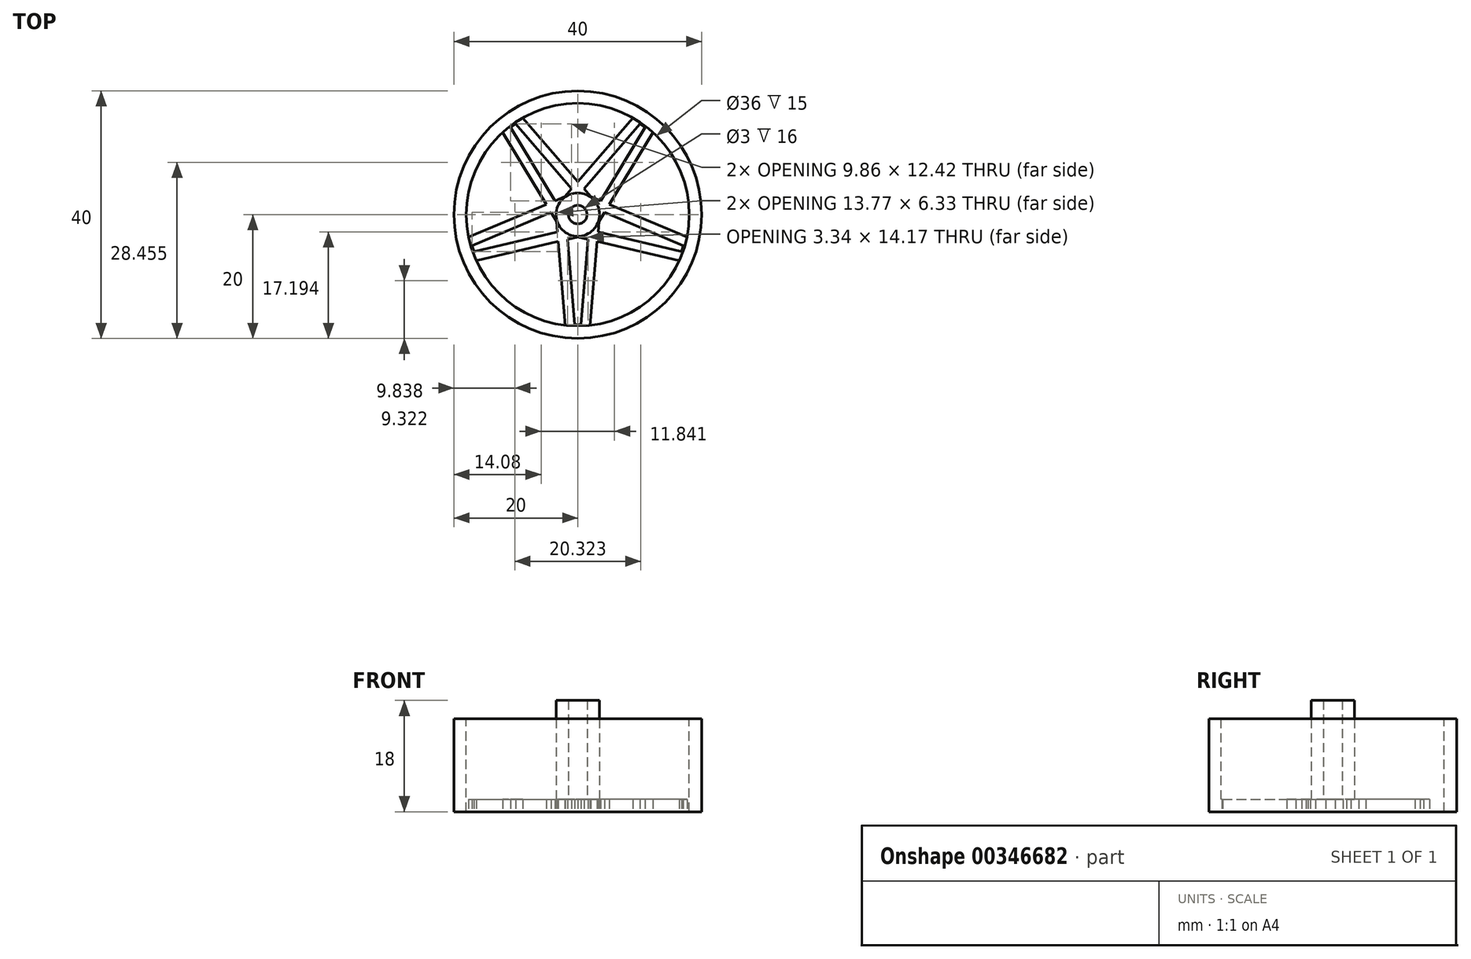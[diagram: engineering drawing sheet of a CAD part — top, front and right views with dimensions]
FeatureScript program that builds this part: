
annotation { "Feature Type Name" : "Feature", "Feature Type Description" : "" }
export const myFeature = defineFeature(function(context is Context, id is Id, definition is map)
    precondition{}
    {
        {
            var Q0;
            Q0=qCreatedBy(makeId("Top.planeOp"),FACE);
            var sketch = newSketch(context, id + "F0", { "sketchPlane" : qUnion([Q0])});
            skCircle(sketch, "E0", {"center": v(0, 0) * mm, "radius": 20 * mm});
            skSolve(sketch);
        }
        {
            var Q0;
            Q0=makeQuery(id+"F0.imprint","IMPRINT",FACE,{"disambiguationData":[TD([[makeQuery(id+"F0.imprint","IMPRINT",EDGE,{"derivedFrom":sQuery(id+"F0.wireOp",EDGE,"E0")}),1.0]])]});
            extrude(context, id + "F1", {"entities" : qUnion([Q0]), "depth" : 15 * mm});
        }
        {
            var Q0;
            Q0=makeQuery(id+"F1.opExtrude","CAP_FACE",FACE,{"disambiguationData":[OSD([sQuery(id+"F0.wireOp",EDGE,"E0")])],"isStart":false});
            var sketch = newSketch(context, id + "F2", { "sketchPlane" : qUnion([Q0])});
            skCircle(sketch, "E1", {"center": v(0, 0) * mm, "radius": 18 * mm});
            skSolve(sketch);
        }
        {
            var Q0;
            Q0=makeQuery(id+"F2.imprint","IMPRINT",FACE,{"disambiguationData":[TD([[makeQuery(id+"F2.imprint","IMPRINT",EDGE,{"derivedFrom":sQuery(id+"F2.wireOp",EDGE,"E1")}),1.0]])]});
            extrude(context, id + "F3", {"entities" : qUnion([Q0]), "operationType" : NewBodyOperationType.REMOVE, "oppositeDirection" : true, "depth" : 13 * mm});
        }
        {
            var Q0;
            Q0=makeQuery(id+"F3.boolean.opBoolean","COPY",FACE,{"derivedFrom":makeQuery(id+"F3.opExtrude","CAP_FACE",FACE,{"disambiguationData":[OSD([sQuery(id+"F2.wireOp",EDGE,"E1")])],"isStart":false})});
            var sketch = newSketch(context, id + "F4", { "sketchPlane" : qUnion([Q0])});
            skCircle(sketch, "E2", {"center": v(0, 0) * mm, "radius": 1.5 * mm});
            skCircle(sketch, "E3", {"center": v(0, 0) * mm, "radius": 3.5 * mm});
            skSolve(sketch);
        }
        {
            var Q0;
            Q0=makeQuery(id+"F1.opExtrude","CAP_FACE",FACE,{"disambiguationData":[OSD([sQuery(id+"F0.wireOp",EDGE,"E0")])],"isStart":true});
            var sketch = newSketch(context, id + "F5", { "sketchPlane" : qUnion([Q0])});
            skArc(sketch, "E4", {"start": v(-2, 17.89) * mm, "mid": v(-10.58, 14.56) * mm, "end": v(-16.4, 7.43) * mm});
            skLineSegment(sketch, "E5", {"start": v(0, 0) * mm, "end": v(2, 0) * mm});
            skLineSegment(sketch, "E6", {"start": v(2, 17.89) * mm, "end": v(3.15, 4.33) * mm});
            skLineSegment(sketch, "E7.MirrorCS", {"start": v(-2, 17.89) * mm, "end": v(-3.15, 4.33) * mm});
            skLineSegment(sketch, "E8.0", {"start": v(-0.5, 17.76) * mm, "end": v(-1.67, 3.99) * mm});
            skLineSegment(sketch, "E9.0", {"start": v(0.5, 17.76) * mm, "end": v(1.67, 3.99) * mm});
            skLineSegment(sketch, "E10", {"start": v(-0.5, 17.76) * mm, "end": v(0.5, 17.76) * mm});
            skLineSegment(sketch, "E11.1.0", {"start": v(-17.63, 3.63) * mm, "end": v(-5.1, -1.65) * mm});
            skLineSegment(sketch, "E11.1.1", {"start": v(-17.05, 5) * mm, "end": v(-4.3, -0.36) * mm});
            skLineSegment(sketch, "E11.1.2", {"start": v(-17.05, 5) * mm, "end": v(-16.74, 5.97) * mm});
            skLineSegment(sketch, "E11.1.3", {"start": v(-16.74, 5.97) * mm, "end": v(-3.27, 2.82) * mm});
            skLineSegment(sketch, "E11.1.4", {"start": v(-16.4, 7.43) * mm, "end": v(-3.15, 4.33) * mm});
            skLineSegment(sketch, "E11.2.0", {"start": v(-8.9, -15.65) * mm, "end": v(0, -5.35) * mm});
            skLineSegment(sketch, "E11.2.1", {"start": v(-10.03, -14.67) * mm, "end": v(-1, -4.2) * mm});
            skLineSegment(sketch, "E11.2.2", {"start": v(-10.03, -14.67) * mm, "end": v(-10.85, -14.07) * mm});
            skLineSegment(sketch, "E11.2.3", {"start": v(-10.85, -14.07) * mm, "end": v(-3.7, -2.24) * mm});
            skLineSegment(sketch, "E11.2.4", {"start": v(-12.13, -13.3) * mm, "end": v(-5.1, -1.65) * mm});
            skLineSegment(sketch, "E11.3.0", {"start": v(12.13, -13.3) * mm, "end": v(5.1, -1.65) * mm});
            skLineSegment(sketch, "E11.3.1", {"start": v(10.85, -14.07) * mm, "end": v(3.7, -2.24) * mm});
            skLineSegment(sketch, "E11.3.2", {"start": v(10.85, -14.07) * mm, "end": v(10.03, -14.67) * mm});
            skLineSegment(sketch, "E11.3.3", {"start": v(10.03, -14.67) * mm, "end": v(1, -4.2) * mm});
            skLineSegment(sketch, "E11.3.4", {"start": v(8.9, -15.65) * mm, "end": v(0, -5.35) * mm});
            skLineSegment(sketch, "E11.4.0", {"start": v(16.4, 7.43) * mm, "end": v(3.15, 4.33) * mm});
            skLineSegment(sketch, "E11.4.1", {"start": v(16.74, 5.97) * mm, "end": v(3.27, 2.82) * mm});
            skLineSegment(sketch, "E11.4.2", {"start": v(16.74, 5.97) * mm, "end": v(17.05, 5) * mm});
            skLineSegment(sketch, "E11.4.3", {"start": v(17.05, 5) * mm, "end": v(4.3, -0.36) * mm});
            skLineSegment(sketch, "E11.4.4", {"start": v(17.63, 3.63) * mm, "end": v(5.1, -1.65) * mm});
            skLineSegment(sketch, "E12.trimOffspring", {"start": v(1.67, 3.99) * mm, "end": v(0, 3.6) * mm});
            skLineSegment(sketch, "E13.trimOffspring", {"start": v(3.27, 2.82) * mm, "end": v(3.42, 1.11) * mm});
            skPoint(sketch, "E14.orphan", {"position": v(2.84, 2.06) * mm});
            skPoint(sketch, "E15.orphan", {"position": v(2.34, 2.6) * mm});
            skLineSegment(sketch, "E16.trimOffspring", {"start": v(-3.27, 2.82) * mm, "end": v(-3.42, 1.11) * mm});
            skLineSegment(sketch, "E17.trimOffspring", {"start": v(-1.67, 3.99) * mm, "end": v(0, 3.6) * mm});
            skLineSegment(sketch, "E18.trimOffspring", {"start": v(-4.3, -0.36) * mm, "end": v(-3.42, 1.11) * mm});
            skLineSegment(sketch, "E19.trimOffspring", {"start": v(-3.7, -2.24) * mm, "end": v(-2.11, -2.9) * mm});
            skLineSegment(sketch, "E20.trimOffspring", {"start": v(1, -4.2) * mm, "end": v(2.11, -2.9) * mm});
            skLineSegment(sketch, "E21.trimOffspring", {"start": v(-1, -4.2) * mm, "end": v(-2.11, -2.9) * mm});
            skPoint(sketch, "E22.orphan", {"position": v(1.09, 3.34) * mm});
            skPoint(sketch, "E23.orphan", {"position": v(-1.09, 3.34) * mm});
            skPoint(sketch, "E24.orphan", {"position": v(-1.75, 3.03) * mm});
            skPoint(sketch, "E25.orphan", {"position": v(-2.34, 2.6) * mm});
            skPoint(sketch, "E26.orphan", {"position": v(-2.84, 2.06) * mm});
            skPoint(sketch, "E27.trimOffspring.end.orphan", {"position": v(-3.51, 0) * mm});
            skPoint(sketch, "E28.orphan", {"position": v(-3.42, -0.73) * mm});
            skPoint(sketch, "E29.orphan", {"position": v(-2.84, -2.06) * mm});
            skPoint(sketch, "E30.trimOffspring.end.orphan", {"position": v(3.51, 0) * mm});
            skPoint(sketch, "E31.orphan", {"position": v(0.36, -3.48) * mm});
            skPoint(sketch, "E32.orphan", {"position": v(3.2, -1.42) * mm});
            skPoint(sketch, "E33.orphan", {"position": v(3.42, -0.73) * mm});
            skLineSegment(sketch, "E34.trimOffspring", {"start": v(4.3, -0.36) * mm, "end": v(3.42, 1.11) * mm});
            skLineSegment(sketch, "E35.trimOffspring", {"start": v(3.7, -2.24) * mm, "end": v(2.11, -2.9) * mm});
            skArc(sketch, "E36.trimOffspring", {"start": v(-17.63, 3.63) * mm, "mid": v(-17.12, -5.56) * mm, "end": v(-12.13, -13.3) * mm});
            skArc(sketch, "E37.trimOffspring", {"start": v(16.4, 7.43) * mm, "mid": v(10.58, 14.56) * mm, "end": v(2, 17.89) * mm});
            skArc(sketch, "E38.trimOffspring", {"start": v(12.13, -13.3) * mm, "mid": v(17.12, -5.56) * mm, "end": v(17.63, 3.63) * mm});
            skArc(sketch, "E39.trimOffspring", {"start": v(-8.9, -15.65) * mm, "mid": v(0, -18) * mm, "end": v(8.9, -15.65) * mm});
            skSolve(sketch);
        }
        {
            var Q0;
            Q0=makeQuery(id+"F5.imprint","IMPRINT",FACE,{"disambiguationData":[TD([[makeQuery(id+"F5.imprint","IMPRINT",EDGE,{"derivedFrom":sQuery(id+"F5.wireOp",EDGE,"E4")}),1.0]])]});
            var Q1;
            Q1=makeQuery(id+"F5.imprint","IMPRINT",FACE,{"disambiguationData":[TD([[makeQuery(id+"F5.imprint","IMPRINT",EDGE,{"derivedFrom":sQuery(id+"F5.wireOp",EDGE,"E8.0")}),1.0]])]});
            var Q2;
            Q2=makeQuery(id+"F5.imprint","IMPRINT",FACE,{"disambiguationData":[TD([[makeQuery(id+"F5.imprint","IMPRINT",EDGE,{"derivedFrom":sQuery(id+"F5.wireOp",EDGE,"E6")}),1.0]])]});
            var Q3;
            Q3=makeQuery(id+"F5.imprint","IMPRINT",FACE,{"disambiguationData":[TD([[makeQuery(id+"F5.imprint","IMPRINT",EDGE,{"derivedFrom":sQuery(id+"F5.wireOp",EDGE,"E11.4.1")}),1.0]])]});
            var Q4;
            Q4=makeQuery(id+"F5.imprint","IMPRINT",FACE,{"disambiguationData":[TD([[makeQuery(id+"F5.imprint","IMPRINT",EDGE,{"derivedFrom":sQuery(id+"F5.wireOp",EDGE,"E11.3.0")}),-1.0]])]});
            var Q5;
            Q5=makeQuery(id+"F5.imprint","IMPRINT",FACE,{"disambiguationData":[TD([[makeQuery(id+"F5.imprint","IMPRINT",EDGE,{"derivedFrom":sQuery(id+"F5.wireOp",EDGE,"E11.3.1")}),1.0]])]});
            var Q6;
            Q6=makeQuery(id+"F5.imprint","IMPRINT",FACE,{"disambiguationData":[TD([[makeQuery(id+"F5.imprint","IMPRINT",EDGE,{"derivedFrom":sQuery(id+"F5.wireOp",EDGE,"E11.2.0")}),-1.0]])]});
            var Q7;
            Q7=makeQuery(id+"F5.imprint","IMPRINT",FACE,{"disambiguationData":[TD([[makeQuery(id+"F5.imprint","IMPRINT",EDGE,{"derivedFrom":sQuery(id+"F5.wireOp",EDGE,"E11.2.1")}),1.0]])]});
            var Q8;
            Q8=makeQuery(id+"F5.imprint","IMPRINT",FACE,{"disambiguationData":[TD([[makeQuery(id+"F5.imprint","IMPRINT",EDGE,{"derivedFrom":sQuery(id+"F5.wireOp",EDGE,"E11.1.0")}),-1.0]])]});
            var Q9;
            Q9=makeQuery(id+"F5.imprint","IMPRINT",FACE,{"disambiguationData":[TD([[makeQuery(id+"F5.imprint","IMPRINT",EDGE,{"derivedFrom":sQuery(id+"F5.wireOp",EDGE,"E11.1.1")}),1.0]])]});
            extrude(context, id + "F6", {"entities" : qUnion([Q0, Q1, Q2, Q3, Q4, Q5, Q6, Q7, Q8, Q9]), "operationType" : NewBodyOperationType.REMOVE, "oppositeDirection" : true, "depth" : 2 * mm});
        }
        {
            var Q0;
            Q0=makeQuery(id+"F4.imprint","IMPRINT",FACE,{"disambiguationData":[TD([[makeQuery(id+"F4.imprint","IMPRINT",EDGE,{"derivedFrom":sQuery(id+"F4.wireOp",EDGE,"E2")}),-1.0]])]});
            extrude(context, id + "F7", {"entities" : qUnion([Q0]), "operationType" : NewBodyOperationType.ADD, "depth" : 16 * mm});
        }
    });
